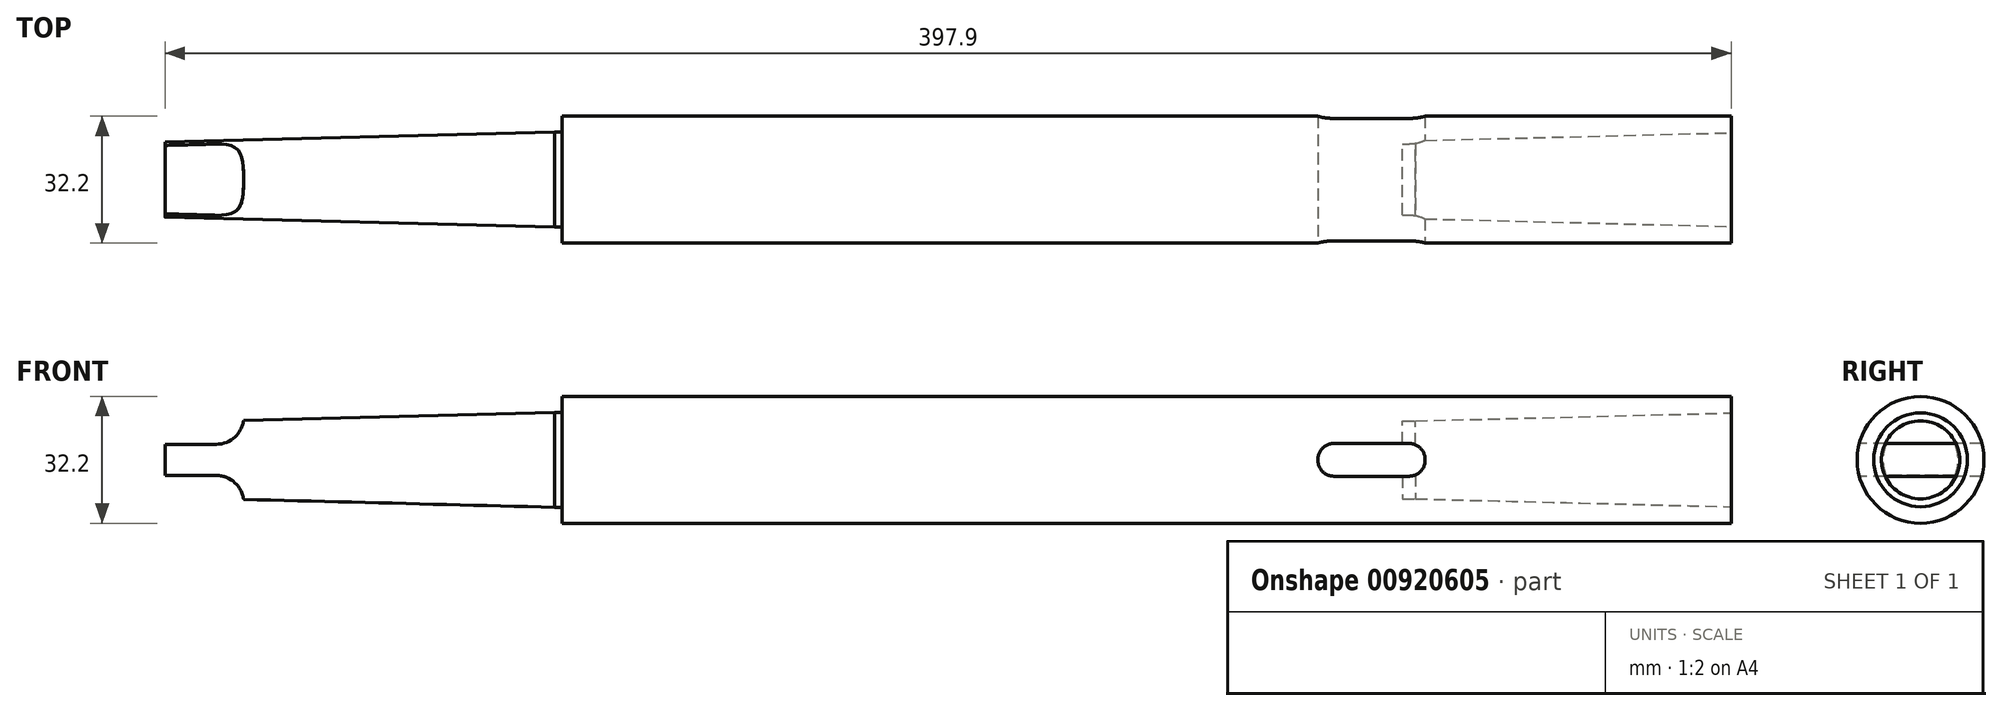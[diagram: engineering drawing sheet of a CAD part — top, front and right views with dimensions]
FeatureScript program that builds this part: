
annotation { "Feature Type Name" : "Feature", "Feature Type Description" : "" }
export const myFeature = defineFeature(function(context is Context, id is Id, definition is map)
    precondition{}
    {
        {
            var Q0;
            Q0=qCreatedBy(makeId("Front.planeOp"),FACE);
            var sketch = newSketch(context, id + "F0", { "sketchPlane" : qUnion([Q0])});
            skLineSegment(sketch, "E0", {"start": v(0, 0) * mm, "end": v(-45.95, 0) * mm, "construction": true});
            skLineSegment(sketch, "E1", {"start": v(5, 12.04) * mm, "end": v(-94, 9.55) * mm});
            skPoint(sketch, "E2", {"position": v(0, 11.91) * mm});
            skLineSegment(sketch, "E3", {"start": v(-94, 9.55) * mm, "end": v(-94, 0) * mm});
            skLineSegment(sketch, "E4", {"start": v(5, 12.04) * mm, "end": v(5, 0) * mm});
            skLineSegment(sketch, "E5", {"start": v(5, 0) * mm, "end": v(-94, 0) * mm});
            skSolve(sketch);
        }
        {
            var Q0;
            Q0=makeQuery(id+"F0.imprint","IMPRINT",FACE,{"disambiguationData":[TD([[makeQuery(id+"F0.imprint","IMPRINT",EDGE,{"derivedFrom":sQuery(id+"F0.wireOp",EDGE,"E1")}),1.0]])]});
            var Q1;
            Q1=sQuery(id+"F0.wireOp",EDGE,"E5");
            revolve(context, id + "F1", {"surfaceOperationType" : NewSurfaceOperationType.NEW, "entities" : qUnion([Q0]), "axis" : qUnion([Q1]), "revolveType" : RevolveType.FULL});
        }
        {
            var Q0;
            Q0=qCreatedBy(makeId("Front.planeOp"),FACE);
            var sketch = newSketch(context, id + "F2", { "sketchPlane" : qUnion([Q0])});
            skLineSegment(sketch, "E6.0", {"start": v(-94, 9.55) * mm, "end": v(-94, -9.55) * mm});
            skLineSegment(sketch, "E7", {"start": v(-94, 9.55) * mm, "end": v(5, 12.04) * mm});
            skLineSegment(sketch, "E8", {"start": v(5, -12.04) * mm, "end": v(-94, -9.55) * mm});
            skLineSegment(sketch, "E9", {"start": v(-94, 3.95) * mm, "end": v(-74, 3.95) * mm});
            skLineSegment(sketch, "E10", {"start": v(-74, 3.95) * mm, "end": v(-74, 10.06) * mm});
            skLineSegment(sketch, "E11", {"start": v(-74, 10.06) * mm, "end": v(-94, 9.55) * mm});
            skLineSegment(sketch, "E12", {"start": v(-94, -3.95) * mm, "end": v(-74, -3.95) * mm});
            skLineSegment(sketch, "E13", {"start": v(-74, -3.95) * mm, "end": v(-74, -10.06) * mm});
            skLineSegment(sketch, "E14", {"start": v(-74, -10.06) * mm, "end": v(-94, -9.55) * mm});
            skLineSegment(sketch, "E15", {"start": v(-94, -9.55) * mm, "end": v(-94, -3.95) * mm});
            skSolve(sketch);
        }
        {
            var Q0;
            {var subQ0=sQuery(id+"F2.wireOp",EDGE,"E9");Q0=makeQuery(id+"F2.imprint","IMPRINT",FACE,{"disambiguationData":[TD([[makeQuery(id+"F2.imprint","IMPRINT",EDGE,{"derivedFrom":subQ0}),1.0]])]});}
            var Q1;
            {var subQ3=sQuery(id+"F2.wireOp",EDGE,"E12");Q1=makeQuery(id+"F2.imprint","IMPRINT",FACE,{"disambiguationData":[TD([[makeQuery(id+"F2.imprint","IMPRINT",EDGE,{"derivedFrom":subQ3}),-1.0]])]});}
            extrude(context, id + "F3", {"entities" : qUnion([Q0, Q1]), "operationType" : NewBodyOperationType.REMOVE, "oppositeDirection" : true, "depth" : 25 * mm, "offsetDistance" : 25 * mm, "symmetric" : true});
        }
        {
            var Q0;
            Q0=makeQuery(id+"F3.boolean.opBoolean","COPY",EDGE,{"derivedFrom":makeQuery(id+"F3.opExtrude","SWEPT_EDGE",EDGE,{"disambiguationData":[OSD([sQuery(id+"F2.wireOp",EDGE,"E12"),sQuery(id+"F2.wireOp",EDGE,"E13")])]})});
            var Q1;
            Q1=makeQuery(id+"F3.boolean.opBoolean","COPY",EDGE,{"derivedFrom":makeQuery(id+"F3.opExtrude","SWEPT_EDGE",EDGE,{"disambiguationData":[OSD([sQuery(id+"F2.wireOp",EDGE,"E9"),sQuery(id+"F2.wireOp",EDGE,"E10")])]})});
            fillet(context, id + "F4", {"entities" : qUnion([Q0, Q1]), "radius" : 7 * mm, "tangentPropagation" : true, "allowEdgeOverflow" : false});
        }
        {
            var Q0;
            Q0=qCreatedBy(makeId("Top.planeOp"),FACE);
            var sketch = newSketch(context, id + "F5", { "sketchPlane" : qUnion([Q0])});
            skLineSegment(sketch, "E16", {"start": v(0, 0) * mm, "end": v(102.78, 0) * mm, "construction": true});
            skLineSegment(sketch, "E17.0", {"start": v(5, 12.04) * mm, "end": v(5, -12.04) * mm, "construction": true});
            skLineSegment(sketch, "E18", {"start": v(-94, 9.55) * mm, "end": v(5, 12.04) * mm, "construction": true});
            skLineSegment(sketch, "E19", {"start": v(5, 12.04) * mm, "end": v(7, 12.04) * mm});
            skLineSegment(sketch, "E20", {"start": v(7, 12.04) * mm, "end": v(6.9, 16.1) * mm});
            skLineSegment(sketch, "E21", {"start": v(6.9, 16.1) * mm, "end": v(303.9, 16.1) * mm});
            skLineSegment(sketch, "E22", {"start": v(303.9, 16.1) * mm, "end": v(303.9, 11.91) * mm});
            skLineSegment(sketch, "E23", {"start": v(303.9, 11.91) * mm, "end": v(223.72, 9.9) * mm});
            skLineSegment(sketch, "E24", {"start": v(220.4, 0) * mm, "end": v(5, 0) * mm});
            skLineSegment(sketch, "E25", {"start": v(5, 0) * mm, "end": v(5, 12.04) * mm});
            skLineSegment(sketch, "E26", {"start": v(223.72, 9.9) * mm, "end": v(220.4, 9.9) * mm});
            skLineSegment(sketch, "E27", {"start": v(220.4, 9.9) * mm, "end": v(220.4, 0) * mm});
            skSolve(sketch);
        }
        {
            var Q0;
            Q0=makeQuery(id+"F5.imprint","IMPRINT",FACE,{"disambiguationData":[TD([[makeQuery(id+"F5.imprint","IMPRINT",EDGE,{"derivedFrom":sQuery(id+"F5.wireOp",EDGE,"E19")}),-1.0]])]});
            var Q1;
            Q1=sQuery(id+"F5.wireOp",EDGE,"E24");
            revolve(context, id + "F6", {"operationType" : NewBodyOperationType.ADD, "surfaceOperationType" : NewSurfaceOperationType.NEW, "entities" : qUnion([Q0]), "axis" : qUnion([Q1]), "revolveType" : RevolveType.FULL});
        }
        {
            var Q0;
            Q0=qCreatedBy(makeId("Front.planeOp"),FACE);
            var sketch = newSketch(context, id + "F7", { "sketchPlane" : qUnion([Q0])});
            skLineSegment(sketch, "E28.bottom", {"start": v(226.1, 4.15) * mm, "end": v(198.9, 4.15) * mm});
            skLineSegment(sketch, "E28.top", {"start": v(226.1, -4.15) * mm, "end": v(198.9, -4.15) * mm});
            skLineSegment(sketch, "E28.left", {"start": v(226.1, 4.15) * mm, "end": v(226.1, -4.15) * mm});
            skLineSegment(sketch, "E28.right", {"start": v(198.9, 4.15) * mm, "end": v(198.9, -4.15) * mm});
            skSolve(sketch);
        }
        {
            var Q0;
            Q0=makeQuery(id+"F7.imprint","IMPRINT",FACE,{"disambiguationData":[TD([[makeQuery(id+"F7.imprint","IMPRINT",EDGE,{"derivedFrom":sQuery(id+"F7.wireOp",EDGE,"E28.bottom")}),1.0]])]});
            extrude(context, id + "F8", {"entities" : qUnion([Q0]), "operationType" : NewBodyOperationType.REMOVE, "oppositeDirection" : true, "depth" : 60 * mm, "offsetDistance" : 25 * mm, "symmetric" : true});
        }
        {
            var Q0;
            Q0=makeQuery(id+"F8.boolean.opBoolean","COPY",EDGE,{"disambiguationData":[OD(1.0)],"derivedFrom":makeQuery(id+"F8.opExtrude","SWEPT_EDGE",EDGE,{"disambiguationData":[OSD([sQuery(id+"F7.wireOp",EDGE,"E28.bottom"),sQuery(id+"F7.wireOp",EDGE,"E28.left")])]})});
            var Q1;
            Q1=makeQuery(id+"F8.boolean.opBoolean","COPY",EDGE,{"disambiguationData":[OD(0.0)],"derivedFrom":makeQuery(id+"F8.opExtrude","SWEPT_EDGE",EDGE,{"disambiguationData":[OSD([sQuery(id+"F7.wireOp",EDGE,"E28.bottom"),sQuery(id+"F7.wireOp",EDGE,"E28.left")])]})});
            var Q2;
            Q2=makeQuery(id+"F8.boolean.opBoolean","COPY",EDGE,{"disambiguationData":[OD(1.0)],"derivedFrom":makeQuery(id+"F8.opExtrude","SWEPT_EDGE",EDGE,{"disambiguationData":[OSD([sQuery(id+"F7.wireOp",EDGE,"E28.top"),sQuery(id+"F7.wireOp",EDGE,"E28.left")])]})});
            var Q3;
            Q3=makeQuery(id+"F8.boolean.opBoolean","COPY",EDGE,{"disambiguationData":[OD(0.0)],"derivedFrom":makeQuery(id+"F8.opExtrude","SWEPT_EDGE",EDGE,{"disambiguationData":[OSD([sQuery(id+"F7.wireOp",EDGE,"E28.top"),sQuery(id+"F7.wireOp",EDGE,"E28.left")])]})});
            var Q4;
            Q4=makeQuery(id+"F8.boolean.opBoolean","COPY",EDGE,{"derivedFrom":makeQuery(id+"F8.opExtrude","SWEPT_EDGE",EDGE,{"disambiguationData":[OSD([sQuery(id+"F7.wireOp",EDGE,"E28.bottom"),sQuery(id+"F7.wireOp",EDGE,"E28.right")])]})});
            var Q5;
            Q5=makeQuery(id+"F8.boolean.opBoolean","COPY",EDGE,{"derivedFrom":makeQuery(id+"F8.opExtrude","SWEPT_EDGE",EDGE,{"disambiguationData":[OSD([sQuery(id+"F7.wireOp",EDGE,"E28.top"),sQuery(id+"F7.wireOp",EDGE,"E28.right")])]})});
            fillet(context, id + "F9", {"entities" : qUnion([Q0, Q1, Q2, Q3, Q4, Q5]), "radius" : 4 * mm, "tangentPropagation" : true, "allowEdgeOverflow" : false});
        }
    });
